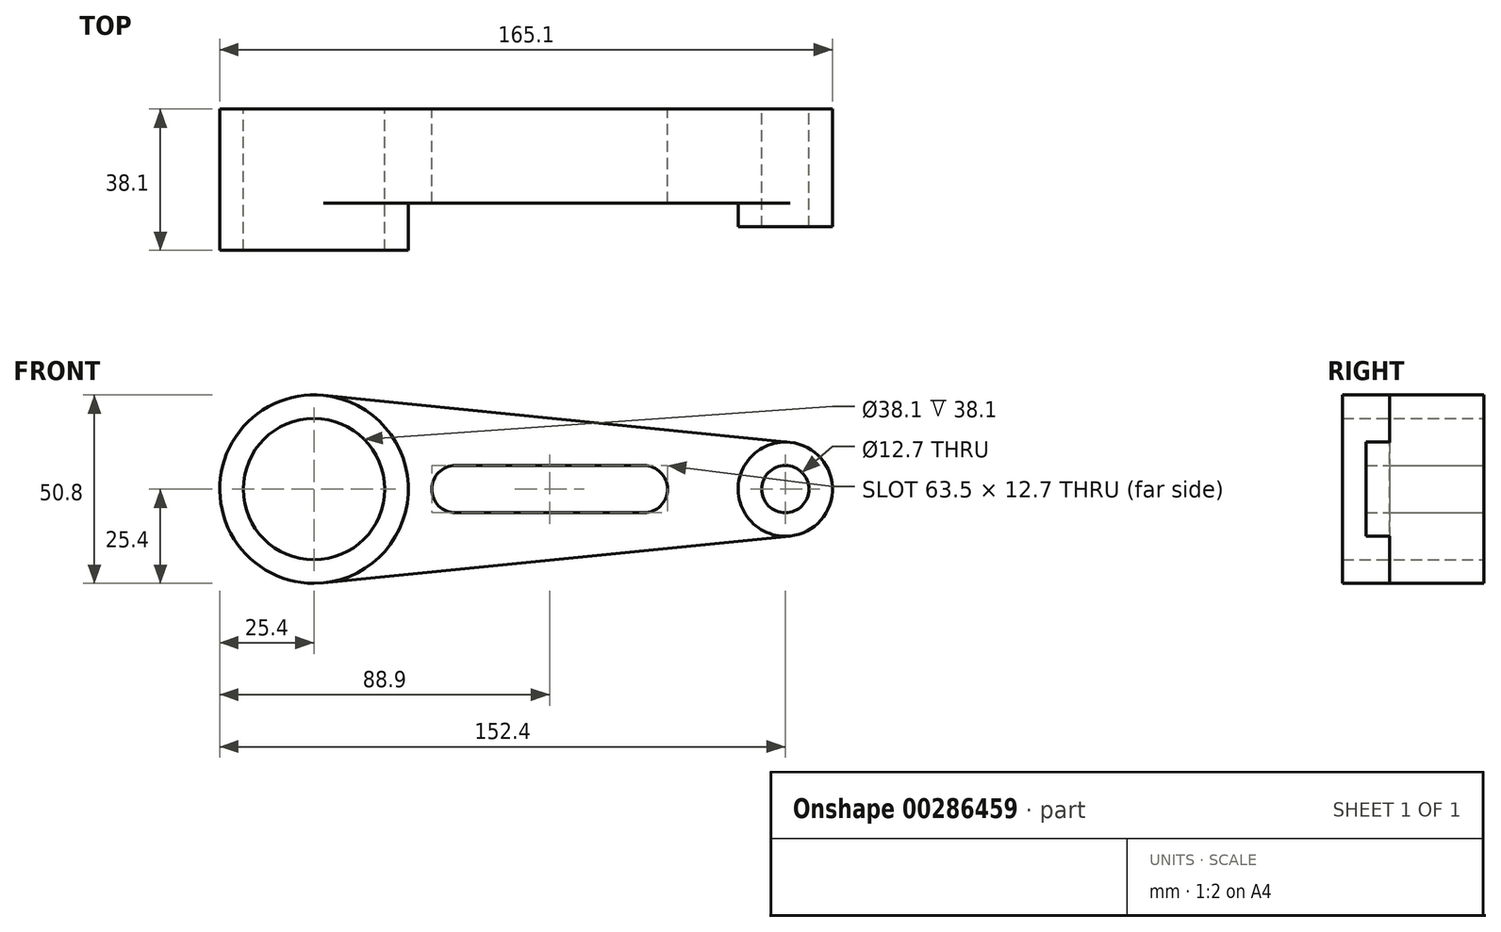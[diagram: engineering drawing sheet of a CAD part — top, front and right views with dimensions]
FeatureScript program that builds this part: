
annotation { "Feature Type Name" : "Feature", "Feature Type Description" : "" }
export const myFeature = defineFeature(function(context is Context, id is Id, definition is map)
    precondition{}
    {
        {
            var Q0;
            Q0=qCreatedBy(makeId("Front.planeOp"),FACE);
            var sketch = newSketch(context, id + "F0", { "sketchPlane" : qUnion([Q0])});
            skCircle(sketch, "E0", {"center": v(-38.1, 0) * mm, "radius": 25.4 * mm});
            skCircle(sketch, "E1", {"center": v(-38.1, 0) * mm, "radius": 19.05 * mm});
            skArc(sketch, "E2", {"start": v(0, 6.35) * mm, "mid": v(-6.35, 0) * mm, "end": v(0, -6.35) * mm});
            skArc(sketch, "E3", {"start": v(50.8, -6.35) * mm, "mid": v(57.15, 0) * mm, "end": v(50.8, 6.35) * mm});
            skCircle(sketch, "E4", {"center": v(88.9, 0) * mm, "radius": 6.35 * mm});
            skCircle(sketch, "E5", {"center": v(88.9, 0) * mm, "radius": 12.7 * mm});
            skLineSegment(sketch, "E6", {"start": v(0, 6.35) * mm, "end": v(50.8, 6.35) * mm});
            skLineSegment(sketch, "E7", {"start": v(0, -6.35) * mm, "end": v(50.8, -6.35) * mm});
            skLineSegment(sketch, "E8", {"start": v(-35.56, 25.27) * mm, "end": v(90.17, 12.64) * mm});
            skLineSegment(sketch, "E9", {"start": v(-35.56, -25.27) * mm, "end": v(90.17, -12.64) * mm});
            skSolve(sketch);
        }
        {
            var Q0;
            Q0=makeQuery(id+"F0.imprint","IMPRINT",FACE,{"disambiguationData":[TD([[makeQuery(id+"F0.imprint","IMPRINT",EDGE,{"derivedFrom":sQuery(id+"F0.wireOp",EDGE,"E1")}),-1.0]])]});
            extrude(context, id + "F1", {"entities" : qUnion([Q0]), "depth" : 38.1 * mm});
        }
        {
            var Q0;
            Q0=makeQuery(id+"F0.imprint","IMPRINT",FACE,{"disambiguationData":[TD([[makeQuery(id+"F0.imprint","IMPRINT",EDGE,{"derivedFrom":sQuery(id+"F0.wireOp",EDGE,"E2")}),-1.0]])]});
            extrude(context, id + "F2", {"entities" : qUnion([Q0]), "operationType" : NewBodyOperationType.ADD, "depth" : 25.4 * mm});
        }
        {
            var Q0;
            Q0=makeQuery(id+"F0.imprint","IMPRINT",FACE,{"disambiguationData":[TD([[makeQuery(id+"F0.imprint","IMPRINT",EDGE,{"derivedFrom":sQuery(id+"F0.wireOp",EDGE,"E4")}),-1.0]])]});
            extrude(context, id + "F3", {"entities" : qUnion([Q0]), "operationType" : NewBodyOperationType.ADD, "depth" : 31.75 * mm});
        }
    });
